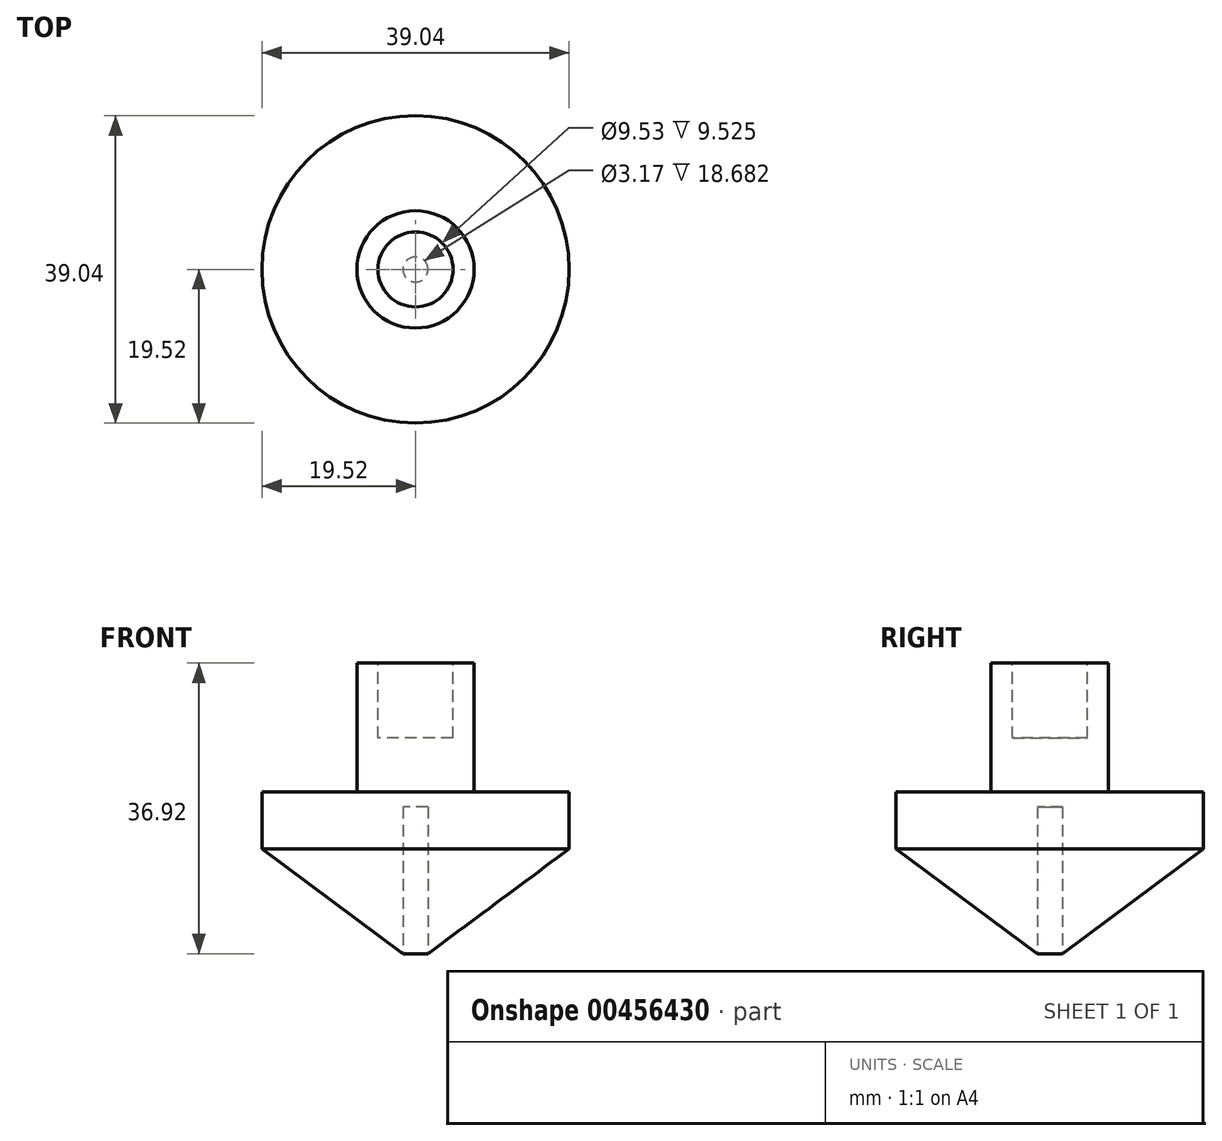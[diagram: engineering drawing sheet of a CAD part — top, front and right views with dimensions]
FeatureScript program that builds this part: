
annotation { "Feature Type Name" : "Feature", "Feature Type Description" : "" }
export const myFeature = defineFeature(function(context is Context, id is Id, definition is map)
    precondition{}
    {
        {
            var Q0;
            Q0=qCreatedBy(makeId("Front.planeOp"),FACE);
            var sketch = newSketch(context, id + "F0", { "sketchPlane" : qUnion([Q0])});
            skLineSegment(sketch, "E0", {"start": v(0, 16.33) * mm, "end": v(7.45, 16.33) * mm});
            skLineSegment(sketch, "E1", {"start": v(7.45, 16.33) * mm, "end": v(7.45, 0) * mm});
            skLineSegment(sketch, "E2", {"start": v(7.45, 0) * mm, "end": v(19.52, 0) * mm});
            skLineSegment(sketch, "E3", {"start": v(19.52, 0) * mm, "end": v(19.52, -7.26) * mm});
            skLineSegment(sketch, "E4", {"start": v(19.52, -7.26) * mm, "end": v(0, -21.77) * mm});
            skLineSegment(sketch, "E5", {"start": v(0, 16.33) * mm, "end": v(0, -21.77) * mm});
            skSolve(sketch);
        }
        {
            var Q0;
            Q0=makeQuery(id+"F0.imprint","IMPRINT",FACE,{"disambiguationData":[TD([[makeQuery(id+"F0.imprint","IMPRINT",EDGE,{"derivedFrom":sQuery(id+"F0.wireOp",EDGE,"E0")}),-1.0]])]});
            var Q1;
            Q1=sQuery(id+"F0.wireOp",EDGE,"E5");
            revolve(context, id + "F1", {"entities" : qUnion([Q0]), "axis" : qUnion([Q1]), "revolveType" : RevolveType.FULL});
        }
        {
            var Q0;
            Q0=makeQuery(id+"F1.opRevolve","SWEPT_FACE",FACE,{"disambiguationData":[OSD([sQuery(id+"F0.wireOp",EDGE,"E0")])]});
            var sketch = newSketch(context, id + "F2", { "sketchPlane" : qUnion([Q0])});
            skCircle(sketch, "E6", {"center": v(0, 0) * mm, "radius": 4.76 * mm});
            skSolve(sketch);
        }
        {
            var Q0;
            Q0 = qSketchRegion(id + "F2", true);
            extrude(context, id + "F3", {"entities" : qUnion([Q0]), "operationType" : NewBodyOperationType.REMOVE, "oppositeDirection" : true, "depth" : 9.52 * mm});
        }
        {
            var Q0;
            Q0=qCreatedBy(makeId("Top.planeOp"),FACE);
            cPlane(context, id + "F4", {"entities" : qUnion([Q0]), "cplaneType" : CPlaneType.OFFSET, "offset" : 22.22 * mm, "oppositeDirection" : true, "width" : 152.4 * mm, "height" : 152.4 * mm});
        }
        {
            var Q0;
            Q0=qCreatedBy(id+"F4.planeOp",FACE);
            var sketch = newSketch(context, id + "F5", { "sketchPlane" : qUnion([Q0])});
            skCircle(sketch, "E7", {"center": v(0, 0) * mm, "radius": 1.59 * mm});
            skSolve(sketch);
        }
        {
            var Q0;
            Q0 = qSketchRegion(id + "F5", true);
            extrude(context, id + "F6", {"entities" : qUnion([Q0]), "operationType" : NewBodyOperationType.REMOVE, "depth" : 20.32 * mm});
        }
    });
